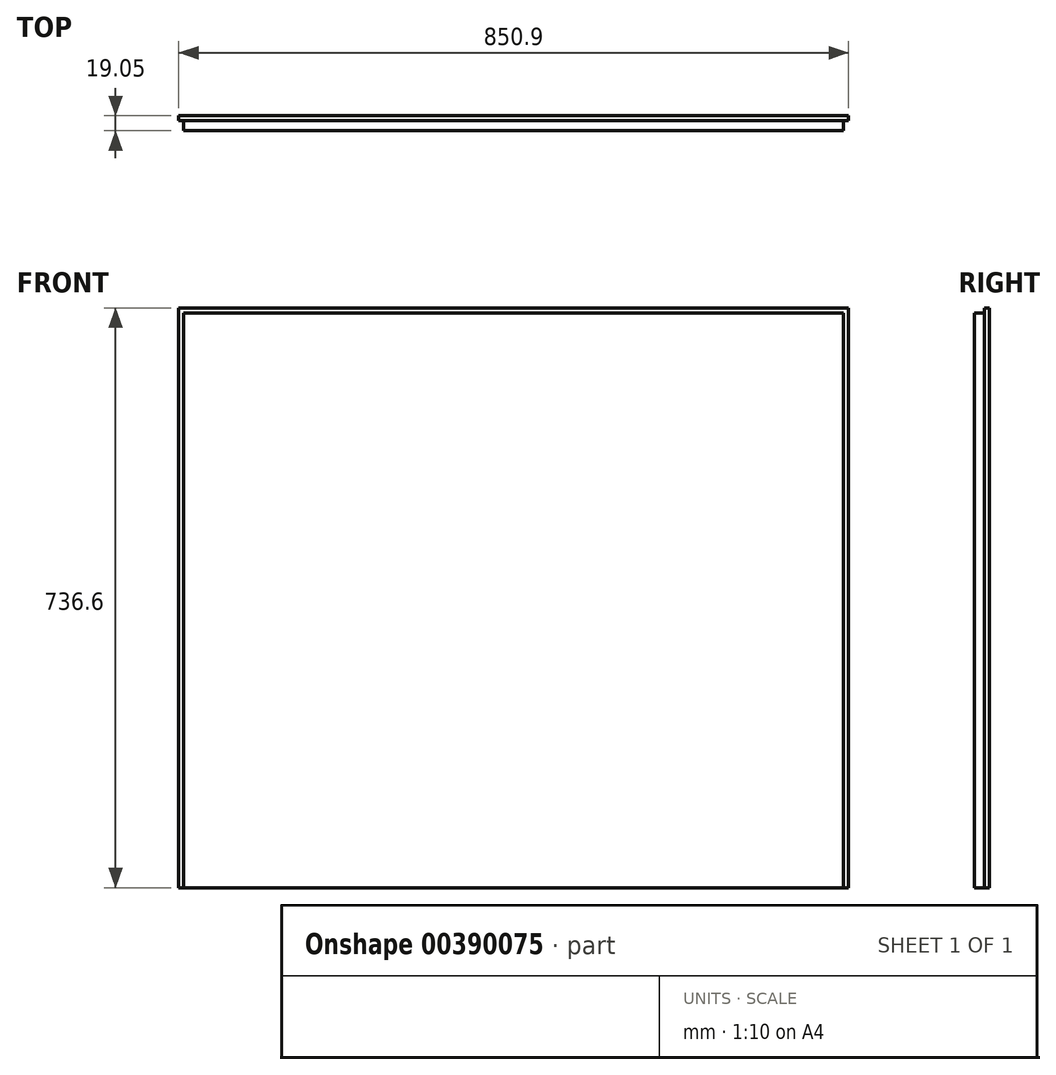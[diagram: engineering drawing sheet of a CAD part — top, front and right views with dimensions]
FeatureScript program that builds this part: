
annotation { "Feature Type Name" : "Feature", "Feature Type Description" : "" }
export const myFeature = defineFeature(function(context is Context, id is Id, definition is map)
    precondition{}
    {
        {
            var Q0;
            Q0=qCreatedBy(makeId("Front.planeOp"),FACE);
            var sketch = newSketch(context, id + "F0", { "sketchPlane" : qUnion([Q0])});
            skLineSegment(sketch, "E0.bottom", {"start": v(0, 0) * mm, "end": v(850.9, 0) * mm});
            skLineSegment(sketch, "E0.top", {"start": v(0, 736.6) * mm, "end": v(850.9, 736.6) * mm});
            skLineSegment(sketch, "E0.left", {"start": v(0, 0) * mm, "end": v(0, 736.6) * mm});
            skLineSegment(sketch, "E0.right", {"start": v(850.9, 0) * mm, "end": v(850.9, 736.6) * mm});
            skSolve(sketch);
        }
        {
            var Q0;
            Q0=makeQuery(id+"F0.imprint","IMPRINT",FACE,{"disambiguationData":[TD([[makeQuery(id+"F0.imprint","IMPRINT",EDGE,{"derivedFrom":sQuery(id+"F0.wireOp",EDGE,"E0.bottom")}),1.0]])]});
            extrude(context, id + "F1", {"entities" : qUnion([Q0]), "depth" : 19.05 * mm});
        }
        {
            var Q0;
            Q0=makeQuery(id+"F1.opExtrude","SWEPT_FACE",FACE,{"disambiguationData":[OSD([sQuery(id+"F0.wireOp",EDGE,"E0.bottom")])]});
            var sketch = newSketch(context, id + "F2", { "sketchPlane" : qUnion([Q0])});
            skLineSegment(sketch, "E1.bottom", {"start": v(0, 19.05) * mm, "end": v(6.35, 19.05) * mm});
            skLineSegment(sketch, "E1.top", {"start": v(0, 6.35) * mm, "end": v(6.35, 6.35) * mm});
            skLineSegment(sketch, "E1.left", {"start": v(0, 19.05) * mm, "end": v(0, 6.35) * mm});
            skLineSegment(sketch, "E1.right", {"start": v(6.35, 19.05) * mm, "end": v(6.35, 6.35) * mm});
            skPoint(sketch, "E2.oppositeSnap0", {"position": v(3.18, 6.35) * mm});
            skLineSegment(sketch, "E2.bottom", {"start": v(850.9, 19.05) * mm, "end": v(844.55, 19.05) * mm});
            skLineSegment(sketch, "E2.top", {"start": v(850.9, 6.35) * mm, "end": v(844.55, 6.35) * mm});
            skLineSegment(sketch, "E2.left", {"start": v(850.9, 19.05) * mm, "end": v(850.9, 6.35) * mm});
            skLineSegment(sketch, "E2.right", {"start": v(844.55, 19.05) * mm, "end": v(844.55, 6.35) * mm});
            skSolve(sketch);
        }
        {
            var Q0;
            Q0=makeQuery(id+"F1.opExtrude","SWEPT_FACE",FACE,{"disambiguationData":[OSD([sQuery(id+"F0.wireOp",EDGE,"E0.right")])]});
            var sketch = newSketch(context, id + "F3", { "sketchPlane" : qUnion([Q0])});
            skLineSegment(sketch, "E3.bottom", {"start": v(-19.05, 736.6) * mm, "end": v(-6.35, 736.6) * mm});
            skLineSegment(sketch, "E3.top", {"start": v(-19.05, 730.25) * mm, "end": v(-6.35, 730.25) * mm});
            skLineSegment(sketch, "E3.left", {"start": v(-19.05, 736.6) * mm, "end": v(-19.05, 730.25) * mm});
            skLineSegment(sketch, "E3.right", {"start": v(-6.35, 736.6) * mm, "end": v(-6.35, 730.25) * mm});
            skSolve(sketch);
        }
        {
            var Q0;
            Q0=makeQuery(id+"F2.imprint","IMPRINT",FACE,{"disambiguationData":[TD([[makeQuery(id+"F2.imprint","IMPRINT",EDGE,{"derivedFrom":sQuery(id+"F2.wireOp",EDGE,"E2.bottom")}),-1.0]])]});
            var Q1;
            Q1=makeQuery(id+"F2.imprint","IMPRINT",FACE,{"disambiguationData":[TD([[makeQuery(id+"F2.imprint","IMPRINT",EDGE,{"derivedFrom":sQuery(id+"F2.wireOp",EDGE,"E1.bottom")}),-1.0]])]});
            extrude(context, id + "F4", {"entities" : qUnion([Q0, Q1]), "operationType" : NewBodyOperationType.REMOVE, "endBound" : BoundingType.THROUGH_ALL, "oppositeDirection" : true, "depth" : 25.4 * mm});
        }
        {
            var Q0;
            Q0=makeQuery(id+"F3.imprint","IMPRINT",FACE,{"disambiguationData":[TD([[makeQuery(id+"F3.imprint","IMPRINT",EDGE,{"derivedFrom":sQuery(id+"F3.wireOp",EDGE,"E3.bottom")}),-1.0]])]});
            extrude(context, id + "F5", {"entities" : qUnion([Q0]), "operationType" : NewBodyOperationType.REMOVE, "endBound" : BoundingType.THROUGH_ALL, "oppositeDirection" : true, "depth" : 25.4 * mm});
        }
    });
